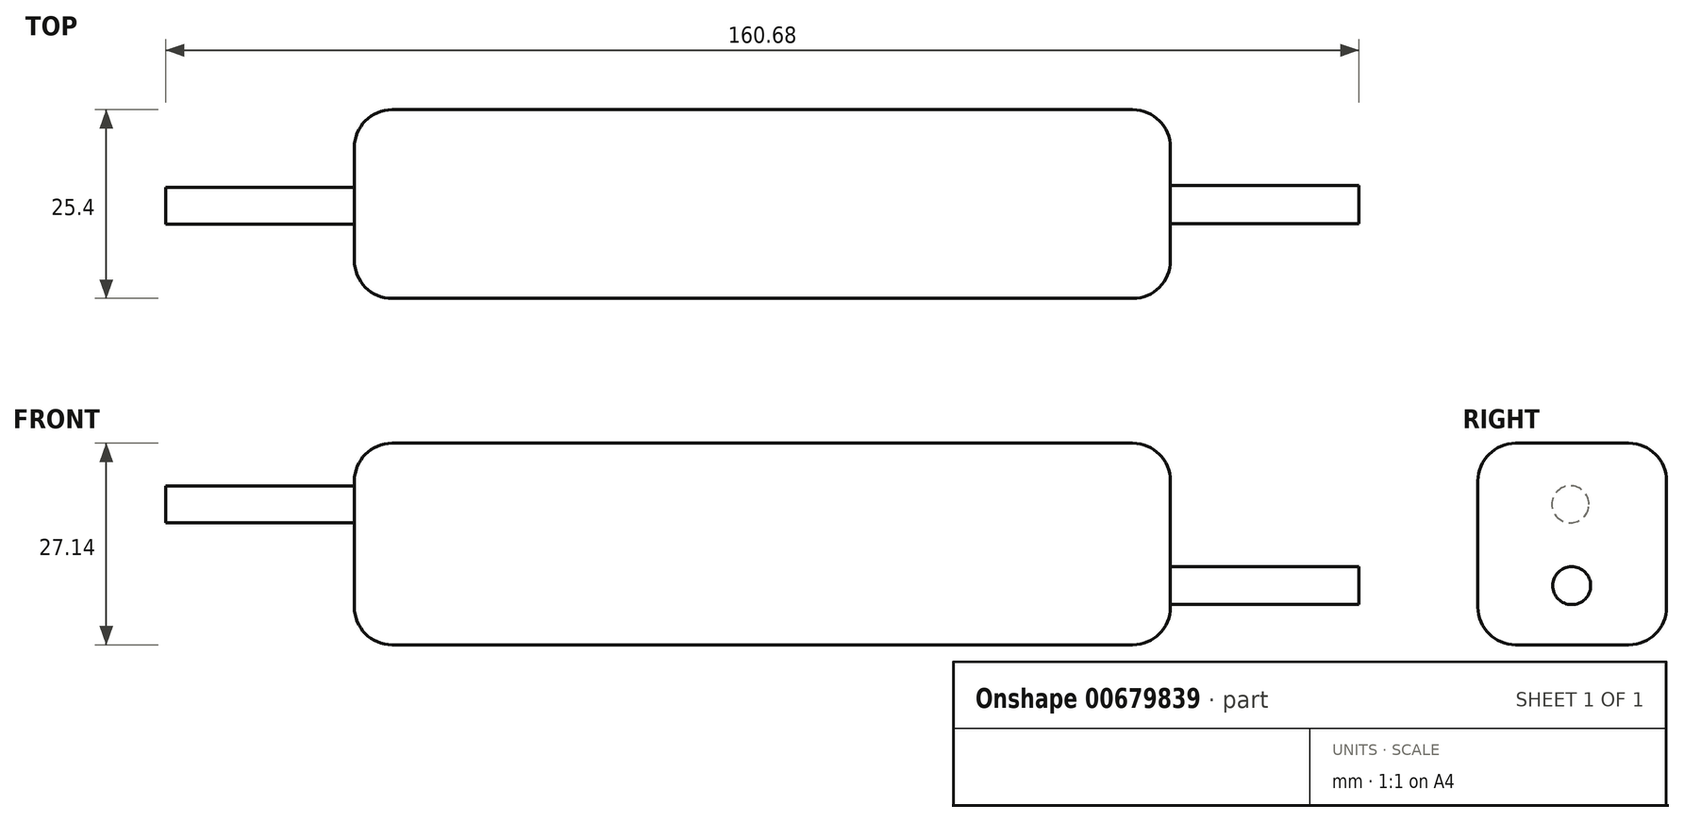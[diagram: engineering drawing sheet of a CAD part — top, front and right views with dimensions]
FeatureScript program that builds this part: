
annotation { "Feature Type Name" : "Feature", "Feature Type Description" : "" }
export const myFeature = defineFeature(function(context is Context, id is Id, definition is map)
    precondition{}
    {
        {
            var Q0;
            Q0=qCreatedBy(makeId("Front.planeOp"),FACE);
            var sketch = newSketch(context, id + "F0", { "sketchPlane" : qUnion([Q0])});
            skLineSegment(sketch, "E0.bottom", {"start": v(32.05, 0) * mm, "end": v(-77.83, 0) * mm});
            skLineSegment(sketch, "E0.top", {"start": v(32.05, 27.14) * mm, "end": v(-77.83, 27.14) * mm});
            skLineSegment(sketch, "E0.left", {"start": v(32.05, 0) * mm, "end": v(32.05, 27.14) * mm});
            skLineSegment(sketch, "E0.right", {"start": v(-77.83, 0) * mm, "end": v(-77.83, 27.14) * mm});
            skPoint(sketch, "E0.middle", {"position": v(-22.89, 13.57) * mm});
            skSolve(sketch);
        }
        {
            var Q0;
            Q0=makeQuery(id+"F0.imprint","IMPRINT",FACE,{"disambiguationData":[TD([[makeQuery(id+"F0.imprint","IMPRINT",EDGE,{"derivedFrom":sQuery(id+"F0.wireOp",EDGE,"E0.bottom")}),-1.0]])]});
            extrude(context, id + "F1", {"entities" : qUnion([Q0]), "depth" : 25.4 * mm, "offsetDistance" : 25.4 * mm});
        }
        {
            var Q0;
            Q0=makeQuery(id+"F1.opExtrude","SWEPT_FACE",FACE,{"disambiguationData":[OSD([sQuery(id+"F0.wireOp",EDGE,"E0.left")])]});
            var sketch = newSketch(context, id + "F2", { "sketchPlane" : qUnion([Q0])});
            skCircle(sketch, "E1", {"center": v(-12.77, 7.97) * mm, "radius": 2.55 * mm});
            skSolve(sketch);
        }
        {
            var Q0;
            Q0 = qSketchRegion(id + "F2", true);
            var Q1;
            Q1=sQuery(id+"F2.wireOp",EDGE,"E1");
            extrude(context, id + "F3", {"entities" : qUnion([Q0]), "surfaceEntities" : qUnion([Q1]), "depth" : 25.4 * mm, "offsetDistance" : 25.4 * mm});
        }
        {
            var Q0;
            Q0=makeQuery(id+"F1.opExtrude","SWEPT_FACE",FACE,{"disambiguationData":[OSD([sQuery(id+"F0.wireOp",EDGE,"E0.right")])]});
            var sketch = newSketch(context, id + "F4", { "sketchPlane" : qUnion([Q0])});
            skCircle(sketch, "E2", {"center": v(12.95, 18.91) * mm, "radius": 2.5 * mm});
            skSolve(sketch);
        }
        {
            var Q0;
            Q0 = qSketchRegion(id + "F4", true);
            var Q1;
            Q1=sQuery(id+"F4.wireOp",EDGE,"E2");
            extrude(context, id + "F5", {"entities" : qUnion([Q0]), "surfaceEntities" : qUnion([Q1]), "depth" : 25.4 * mm, "offsetDistance" : 25.4 * mm});
        }
        {
            var Q0;
            Q0=makeQuery(id+"F1.opExtrude","CAP_EDGE",EDGE,{"disambiguationData":[OSD([sQuery(id+"F0.wireOp",EDGE,"E0.top")])],"isStart":false});
            var Q1;
            Q1=makeQuery(id+"F1.opExtrude","SWEPT_EDGE",EDGE,{"disambiguationData":[OSD([sQuery(id+"F0.wireOp",EDGE,"E0.top"),sQuery(id+"F0.wireOp",EDGE,"E0.left")])]});
            var Q2;
            Q2=makeQuery(id+"F1.opExtrude","CAP_EDGE",EDGE,{"disambiguationData":[OSD([sQuery(id+"F0.wireOp",EDGE,"E0.left")])],"isStart":false});
            var Q3;
            Q3=makeQuery(id+"F1.opExtrude","CAP_EDGE",EDGE,{"disambiguationData":[OSD([sQuery(id+"F0.wireOp",EDGE,"E0.top")])],"isStart":true});
            var Q4;
            Q4=makeQuery(id+"F1.opExtrude","SWEPT_EDGE",EDGE,{"disambiguationData":[OSD([sQuery(id+"F0.wireOp",EDGE,"E0.top"),sQuery(id+"F0.wireOp",EDGE,"E0.right")])]});
            var Q5;
            Q5=makeQuery(id+"F1.opExtrude","CAP_EDGE",EDGE,{"disambiguationData":[OSD([sQuery(id+"F0.wireOp",EDGE,"E0.right")])],"isStart":false});
            var Q6;
            Q6=makeQuery(id+"F1.opExtrude","CAP_EDGE",EDGE,{"disambiguationData":[OSD([sQuery(id+"F0.wireOp",EDGE,"E0.bottom")])],"isStart":false});
            var Q7;
            Q7=makeQuery(id+"F1.opExtrude","CAP_EDGE",EDGE,{"disambiguationData":[OSD([sQuery(id+"F0.wireOp",EDGE,"E0.left")])],"isStart":true});
            var Q8;
            Q8=makeQuery(id+"F1.opExtrude","SWEPT_EDGE",EDGE,{"disambiguationData":[OSD([sQuery(id+"F0.wireOp",EDGE,"E0.bottom"),sQuery(id+"F0.wireOp",EDGE,"E0.left")])]});
            var Q9;
            Q9=makeQuery(id+"F1.opExtrude","CAP_EDGE",EDGE,{"disambiguationData":[OSD([sQuery(id+"F0.wireOp",EDGE,"E0.right")])],"isStart":true});
            var Q10;
            Q10=makeQuery(id+"F1.opExtrude","SWEPT_EDGE",EDGE,{"disambiguationData":[OSD([sQuery(id+"F0.wireOp",EDGE,"E0.bottom"),sQuery(id+"F0.wireOp",EDGE,"E0.right")])]});
            var Q11;
            Q11=makeQuery(id+"F1.opExtrude","CAP_EDGE",EDGE,{"disambiguationData":[OSD([sQuery(id+"F0.wireOp",EDGE,"E0.bottom")])],"isStart":true});
            fillet(context, id + "F6", {"entities" : qUnion([Q0, Q1, Q2, Q3, Q4, Q5, Q6, Q7, Q8, Q9, Q10, Q11]), "radius" : 5.08 * mm, "tangentPropagation" : true, "allowEdgeOverflow" : false});
        }
    });
